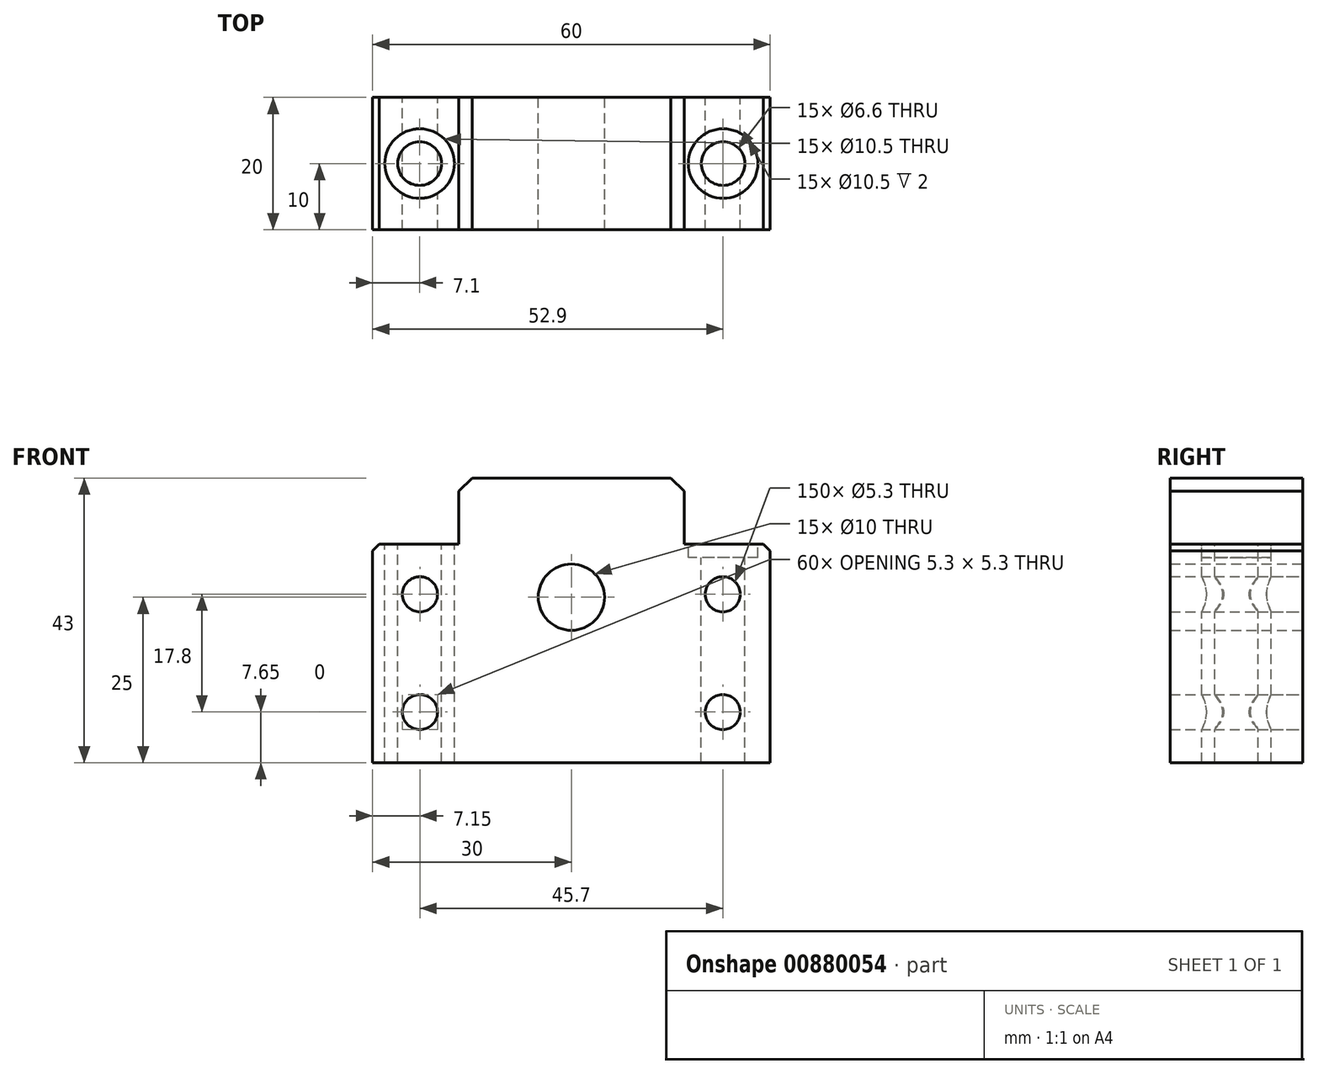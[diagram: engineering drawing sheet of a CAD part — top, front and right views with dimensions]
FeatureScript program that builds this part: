
annotation { "Feature Type Name" : "Feature", "Feature Type Description" : "" }
export const myFeature = defineFeature(function(context is Context, id is Id, definition is map)
    precondition{}
    {
        {
            var Q0;
            Q0=qCreatedBy(makeId("Front.planeOp"),FACE);
            var sketch = newSketch(context, id + "F0", { "sketchPlane" : qUnion([Q0])});
            skLineSegment(sketch, "E0", {"start": v(0, 18) * mm, "end": v(17, 18) * mm});
            skLineSegment(sketch, "E1", {"start": v(17, 18) * mm, "end": v(17, 8) * mm});
            skLineSegment(sketch, "E2", {"start": v(17, 8) * mm, "end": v(30, 8) * mm});
            skLineSegment(sketch, "E3", {"start": v(30, 8) * mm, "end": v(30, -25) * mm});
            skLineSegment(sketch, "E4", {"start": v(30, -25) * mm, "end": v(0, -25) * mm});
            skCircle(sketch, "E5", {"center": v(0, 0) * mm, "radius": 5 * mm});
            skCircle(sketch, "E6", {"center": v(22.85, 0.45) * mm, "radius": 2.65 * mm});
            skCircle(sketch, "E7", {"center": v(22.85, -17.35) * mm, "radius": 2.65 * mm});
            skLineSegment(sketch, "E8.MirrorCS", {"start": v(-17, 8) * mm, "end": v(-30, 8) * mm});
            skLineSegment(sketch, "E9.MirrorCS", {"start": v(0, 18) * mm, "end": v(-17, 18) * mm});
            skLineSegment(sketch, "E10.MirrorCS", {"start": v(-17, 18) * mm, "end": v(-17, 8) * mm});
            skCircle(sketch, "E11.MirrorC", {"center": v(-22.85, -17.35) * mm, "radius": 2.65 * mm});
            skCircle(sketch, "E12.MirrorC", {"center": v(-22.85, 0.45) * mm, "radius": 2.65 * mm});
            skLineSegment(sketch, "E13.MirrorCS", {"start": v(-30, 8) * mm, "end": v(-30, -25) * mm});
            skLineSegment(sketch, "E14.MirrorCS", {"start": v(-30, -25) * mm, "end": v(0, -25) * mm});
            skLineSegment(sketch, "E15", {"start": v(-25.5, -17.35) * mm, "end": v(-30, -17.35) * mm, "construction": true});
            skLineSegment(sketch, "E16", {"start": v(-22.85, -20) * mm, "end": v(-22.85, -25) * mm, "construction": true});
            skLineSegment(sketch, "E17", {"start": v(-22.85, -2.2) * mm, "end": v(-22.85, -14.7) * mm, "construction": true});
            skSolve(sketch);
        }
        {
            var Q0;
            Q0=makeQuery(id+"F0.imprint","IMPRINT",FACE,{"disambiguationData":[TD([[makeQuery(id+"F0.imprint","IMPRINT",EDGE,{"derivedFrom":sQuery(id+"F0.wireOp",EDGE,"E0")}),-1.0]])]});
            extrude(context, id + "F1", {"entities" : qUnion([Q0]), "endBound" : BoundingType.SYMMETRIC, "depth" : 20 * mm});
        }
        {
            var Q0;
            Q0=makeQuery(id+"F1.opExtrude","SWEPT_EDGE",EDGE,{"disambiguationData":[OSD([sQuery(id+"F0.wireOp",EDGE,"E2"),sQuery(id+"F0.wireOp",EDGE,"E3")])]});
            var Q1;
            Q1=makeQuery(id+"F1.opExtrude","SWEPT_EDGE",EDGE,{"disambiguationData":[OSD([sQuery(id+"F0.wireOp",EDGE,"E8.MirrorCS"),sQuery(id+"F0.wireOp",EDGE,"E13.MirrorCS")])]});
            chamfer(context, id + "F2", {"entities" : qUnion([Q0, Q1]), "width" : 1 * mm, "tangentPropagation" : true});
        }
        {
            var Q0;
            Q0=makeQuery(id+"F1.opExtrude","SWEPT_EDGE",EDGE,{"disambiguationData":[OSD([sQuery(id+"F0.wireOp",EDGE,"E0"),sQuery(id+"F0.wireOp",EDGE,"E1")])]});
            var Q1;
            Q1=makeQuery(id+"F1.opExtrude","SWEPT_EDGE",EDGE,{"disambiguationData":[OSD([sQuery(id+"F0.wireOp",EDGE,"E9.MirrorCS"),sQuery(id+"F0.wireOp",EDGE,"E10.MirrorCS")])]});
            chamfer(context, id + "F3", {"entities" : qUnion([Q0, Q1]), "width" : 2 * mm, "tangentPropagation" : true});
        }
        {
            var Q0;
            Q0=makeQuery(id+"F1.opExtrude","SWEPT_FACE",FACE,{"disambiguationData":[OSD([sQuery(id+"F0.wireOp",EDGE,"E2")])]});
            var sketch = newSketch(context, id + "F4", { "sketchPlane" : qUnion([Q0])});
            skCircle(sketch, "E18", {"center": v(22.9, 0) * mm, "radius": 5.25 * mm});
            skCircle(sketch, "E19.MirrorC", {"center": v(-22.9, 0) * mm, "radius": 5.25 * mm});
            skCircle(sketch, "E20", {"center": v(22.9, 0) * mm, "radius": 3.3 * mm});
            skCircle(sketch, "E21.MirrorC", {"center": v(-22.9, 0) * mm, "radius": 3.3 * mm});
            skSolve(sketch);
        }
        {
            var Q0;
            Q0=makeQuery(id+"F4.imprint","IMPRINT",FACE,{"disambiguationData":[TD([[makeQuery(id+"F4.imprint","IMPRINT",EDGE,{"derivedFrom":sQuery(id+"F4.wireOp",EDGE,"E21.MirrorC")}),-1.0]])]});
            var Q1;
            Q1=makeQuery(id+"F4.imprint","IMPRINT",FACE,{"disambiguationData":[TD([[makeQuery(id+"F4.imprint","IMPRINT",EDGE,{"derivedFrom":sQuery(id+"F4.wireOp",EDGE,"E20")}),1.0]])]});
            var Q2;
            Q2=makeQuery(id+"F1.opExtrude","SWEPT_FACE",FACE,{"disambiguationData":[OSD([sQuery(id+"F0.wireOp",EDGE,"E4"),sQuery(id+"F0.wireOp",EDGE,"E14.MirrorCS")])]});
            extrude(context, id + "F5", {"entities" : qUnion([Q0, Q1]), "operationType" : NewBodyOperationType.REMOVE, "endBound" : BoundingType.UP_TO_SURFACE, "oppositeDirection" : true, "endBoundEntityFace" : qUnion([Q2]), "depth" : 25 * mm});
        }
        {
            var Q0;
            Q0=makeQuery(id+"F4.imprint","IMPRINT",FACE,{"disambiguationData":[TD([[makeQuery(id+"F4.imprint","IMPRINT",EDGE,{"derivedFrom":sQuery(id+"F4.wireOp",EDGE,"E18")}),1.0]])]});
            var Q1;
            Q1=makeQuery(id+"F4.imprint","IMPRINT",FACE,{"disambiguationData":[TD([[makeQuery(id+"F4.imprint","IMPRINT",EDGE,{"derivedFrom":sQuery(id+"F4.wireOp",EDGE,"E19.MirrorC")}),-1.0]])]});
            extrude(context, id + "F6", {"entities" : qUnion([Q0, Q1]), "operationType" : NewBodyOperationType.REMOVE, "oppositeDirection" : true, "depth" : 2 * mm});
        }
    });
